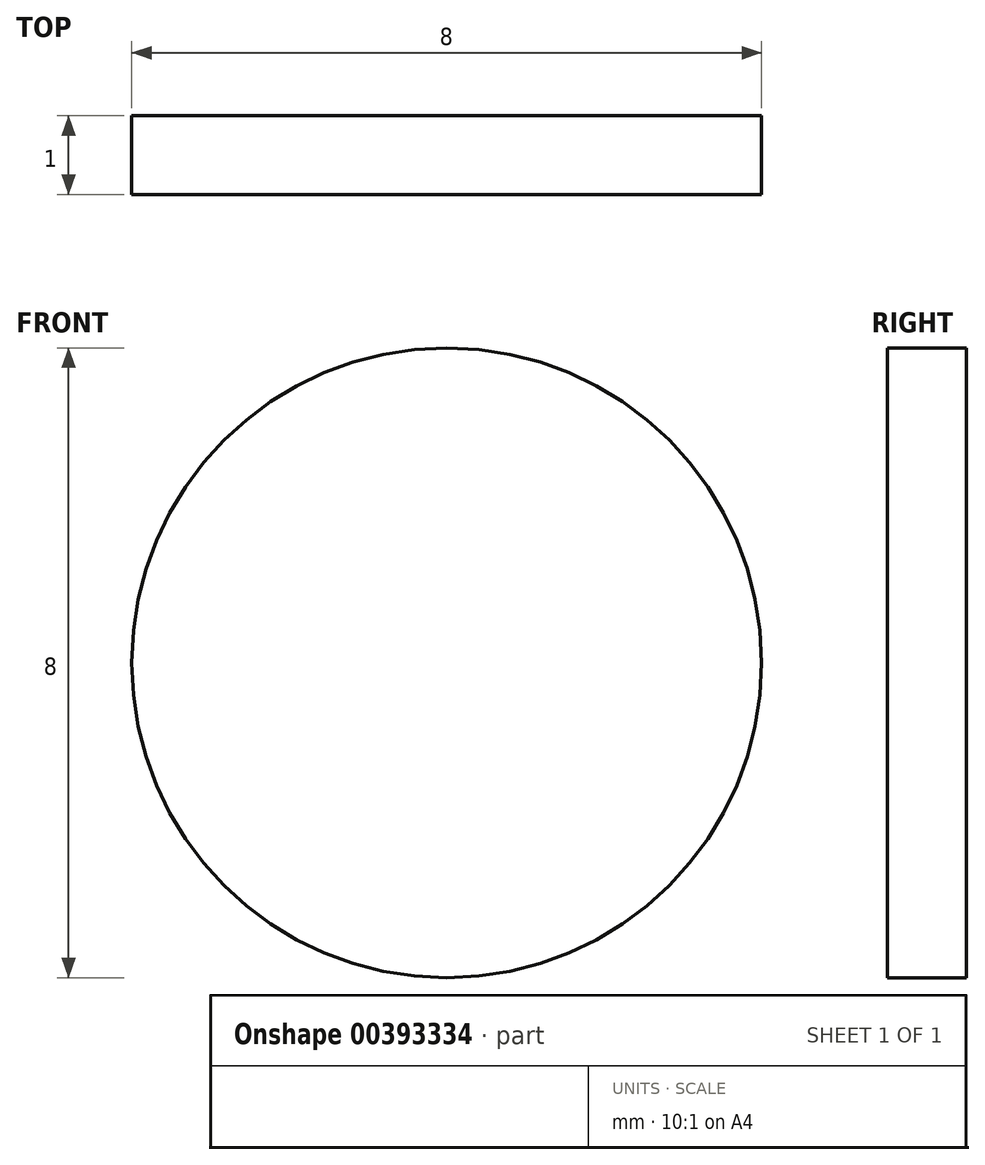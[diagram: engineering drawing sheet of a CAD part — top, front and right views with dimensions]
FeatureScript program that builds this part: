
annotation { "Feature Type Name" : "Feature", "Feature Type Description" : "" }
export const myFeature = defineFeature(function(context is Context, id is Id, definition is map)
    precondition{}
    {
        {
            var Q0;
            Q0=qCreatedBy(makeId("Front.planeOp"),FACE);
            var sketch = newSketch(context, id + "F0", { "sketchPlane" : qUnion([Q0])});
            skCircle(sketch, "E0", {"center": v(0, 0) * mm, "radius": 4 * mm});
            skSolve(sketch);
        }
        {
            var Q0;
            Q0 = qSketchRegion(id + "F0", true);
            extrude(context, id + "F1", {"entities" : qUnion([Q0]), "endBound" : BoundingType.SYMMETRIC, "depth" : 1 * mm});
        }
    });
